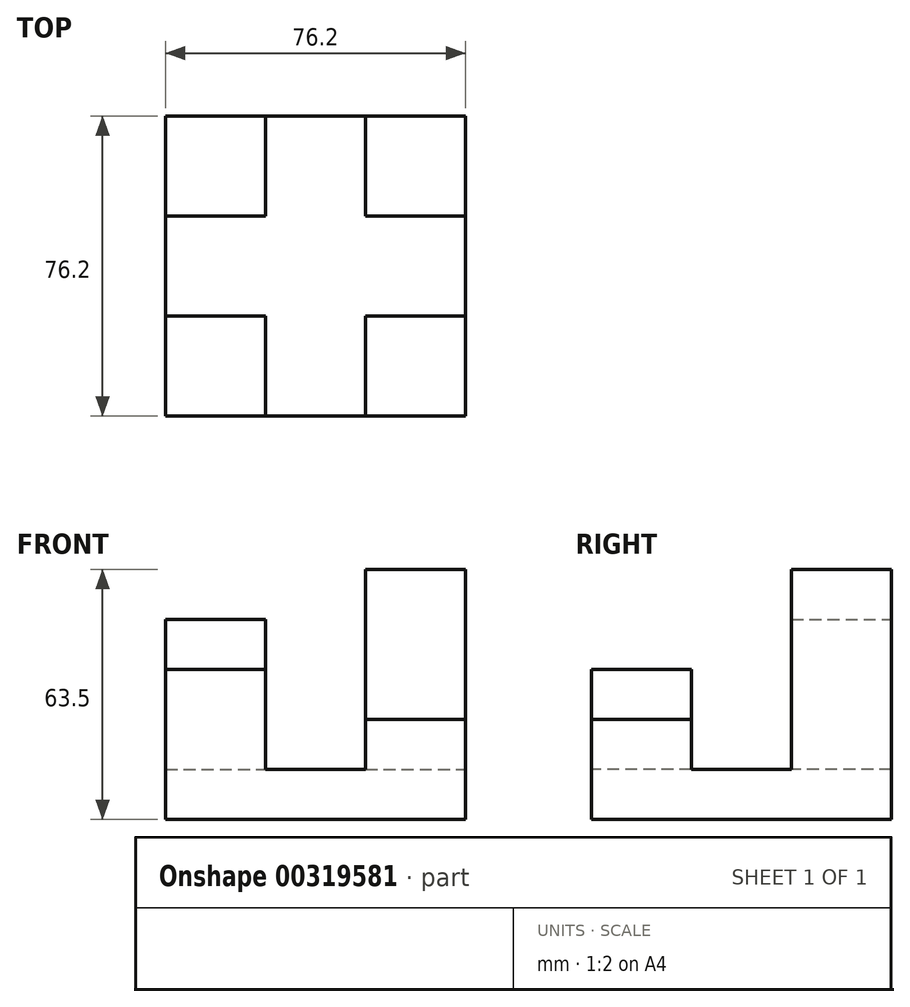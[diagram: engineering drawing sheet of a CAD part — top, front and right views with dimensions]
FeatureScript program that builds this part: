
annotation { "Feature Type Name" : "Feature", "Feature Type Description" : "" }
export const myFeature = defineFeature(function(context is Context, id is Id, definition is map)
    precondition{}
    {
        {
            var Q0;
            Q0=qCreatedBy(makeId("Front.planeOp"),FACE);
            var sketch = newSketch(context, id + "F0", { "sketchPlane" : qUnion([Q0])});
            skLineSegment(sketch, "E0", {"start": v(-47.33, -56.34) * mm, "end": v(28.87, -56.34) * mm});
            skLineSegment(sketch, "E1", {"start": v(28.87, -56.34) * mm, "end": v(28.87, -43.64) * mm});
            skLineSegment(sketch, "E2", {"start": v(28.87, -43.64) * mm, "end": v(-47.33, -43.64) * mm});
            skLineSegment(sketch, "E3", {"start": v(-47.33, -43.64) * mm, "end": v(-47.33, -56.34) * mm});
            skSolve(sketch);
        }
        {
            var Q0;
            Q0=makeQuery(id+"F0.imprint","IMPRINT",FACE,{"disambiguationData":[TD([[makeQuery(id+"F0.imprint","IMPRINT",EDGE,{"derivedFrom":sQuery(id+"F0.wireOp",EDGE,"E0")}),1.0]])]});
            extrude(context, id + "F1", {"entities" : qUnion([Q0]), "depth" : 76.2 * mm});
        }
        {
            var Q0;
            Q0=makeQuery(id+"F1.opExtrude","SWEPT_FACE",FACE,{"disambiguationData":[OSD([sQuery(id+"F0.wireOp",EDGE,"E2")])]});
            var sketch = newSketch(context, id + "F2", { "sketchPlane" : qUnion([Q0])});
            skLineSegment(sketch, "E4", {"start": v(-47.33, -76.2) * mm, "end": v(-47.33, -50.8) * mm});
            skLineSegment(sketch, "E5", {"start": v(-47.33, -50.8) * mm, "end": v(-21.93, -50.8) * mm});
            skLineSegment(sketch, "E6", {"start": v(-21.93, -50.8) * mm, "end": v(-21.93, -76.2) * mm});
            skLineSegment(sketch, "E7", {"start": v(-21.93, -76.2) * mm, "end": v(-47.33, -76.2) * mm});
            skLineSegment(sketch, "E8", {"start": v(28.87, -76.2) * mm, "end": v(3.47, -76.2) * mm});
            skLineSegment(sketch, "E9", {"start": v(3.47, -76.2) * mm, "end": v(3.47, -50.8) * mm});
            skLineSegment(sketch, "E10", {"start": v(3.47, -50.8) * mm, "end": v(28.87, -50.8) * mm});
            skLineSegment(sketch, "E11", {"start": v(28.87, -50.8) * mm, "end": v(28.87, -76.2) * mm});
            skLineSegment(sketch, "E12", {"start": v(28.87, 0) * mm, "end": v(3.47, 0) * mm});
            skLineSegment(sketch, "E13", {"start": v(3.47, 0) * mm, "end": v(3.47, -25.4) * mm});
            skLineSegment(sketch, "E14", {"start": v(3.47, -25.4) * mm, "end": v(28.87, -25.4) * mm});
            skLineSegment(sketch, "E15", {"start": v(28.87, -25.4) * mm, "end": v(28.87, 0) * mm});
            skLineSegment(sketch, "E16", {"start": v(-47.33, 0) * mm, "end": v(-47.33, -25.4) * mm});
            skLineSegment(sketch, "E17", {"start": v(-47.33, -25.4) * mm, "end": v(-21.93, -25.4) * mm});
            skLineSegment(sketch, "E18", {"start": v(-21.93, -25.4) * mm, "end": v(-21.93, 0) * mm});
            skLineSegment(sketch, "E19", {"start": v(-21.93, 0) * mm, "end": v(-47.33, 0) * mm});
            skSolve(sketch);
        }
        {
            var Q0;
            Q0=makeQuery(id+"F2.imprint","IMPRINT",FACE,{"disambiguationData":[TD([[makeQuery(id+"F2.imprint","IMPRINT",EDGE,{"derivedFrom":sQuery(id+"F2.wireOp",EDGE,"E8")}),-1.0]])]});
            extrude(context, id + "F3", {"entities" : qUnion([Q0]), "operationType" : NewBodyOperationType.ADD, "depth" : 12.7 * mm});
        }
        {
            var Q0;
            Q0=makeQuery(id+"F2.imprint","IMPRINT",FACE,{"disambiguationData":[TD([[makeQuery(id+"F2.imprint","IMPRINT",EDGE,{"derivedFrom":sQuery(id+"F2.wireOp",EDGE,"E4")}),-1.0]])]});
            extrude(context, id + "F4", {"entities" : qUnion([Q0]), "operationType" : NewBodyOperationType.ADD, "depth" : 25.4 * mm});
        }
        {
            var Q0;
            Q0=makeQuery(id+"F2.imprint","IMPRINT",FACE,{"disambiguationData":[TD([[makeQuery(id+"F2.imprint","IMPRINT",EDGE,{"derivedFrom":sQuery(id+"F2.wireOp",EDGE,"E16")}),-1.0]])]});
            extrude(context, id + "F5", {"entities" : qUnion([Q0]), "operationType" : NewBodyOperationType.ADD, "depth" : 38.1 * mm});
        }
        {
            var Q0;
            Q0=makeQuery(id+"F2.imprint","IMPRINT",FACE,{"disambiguationData":[TD([[makeQuery(id+"F2.imprint","IMPRINT",EDGE,{"derivedFrom":sQuery(id+"F2.wireOp",EDGE,"E12")}),1.0]])]});
            extrude(context, id + "F6", {"entities" : qUnion([Q0]), "operationType" : NewBodyOperationType.ADD, "depth" : 50.8 * mm});
        }
    });
